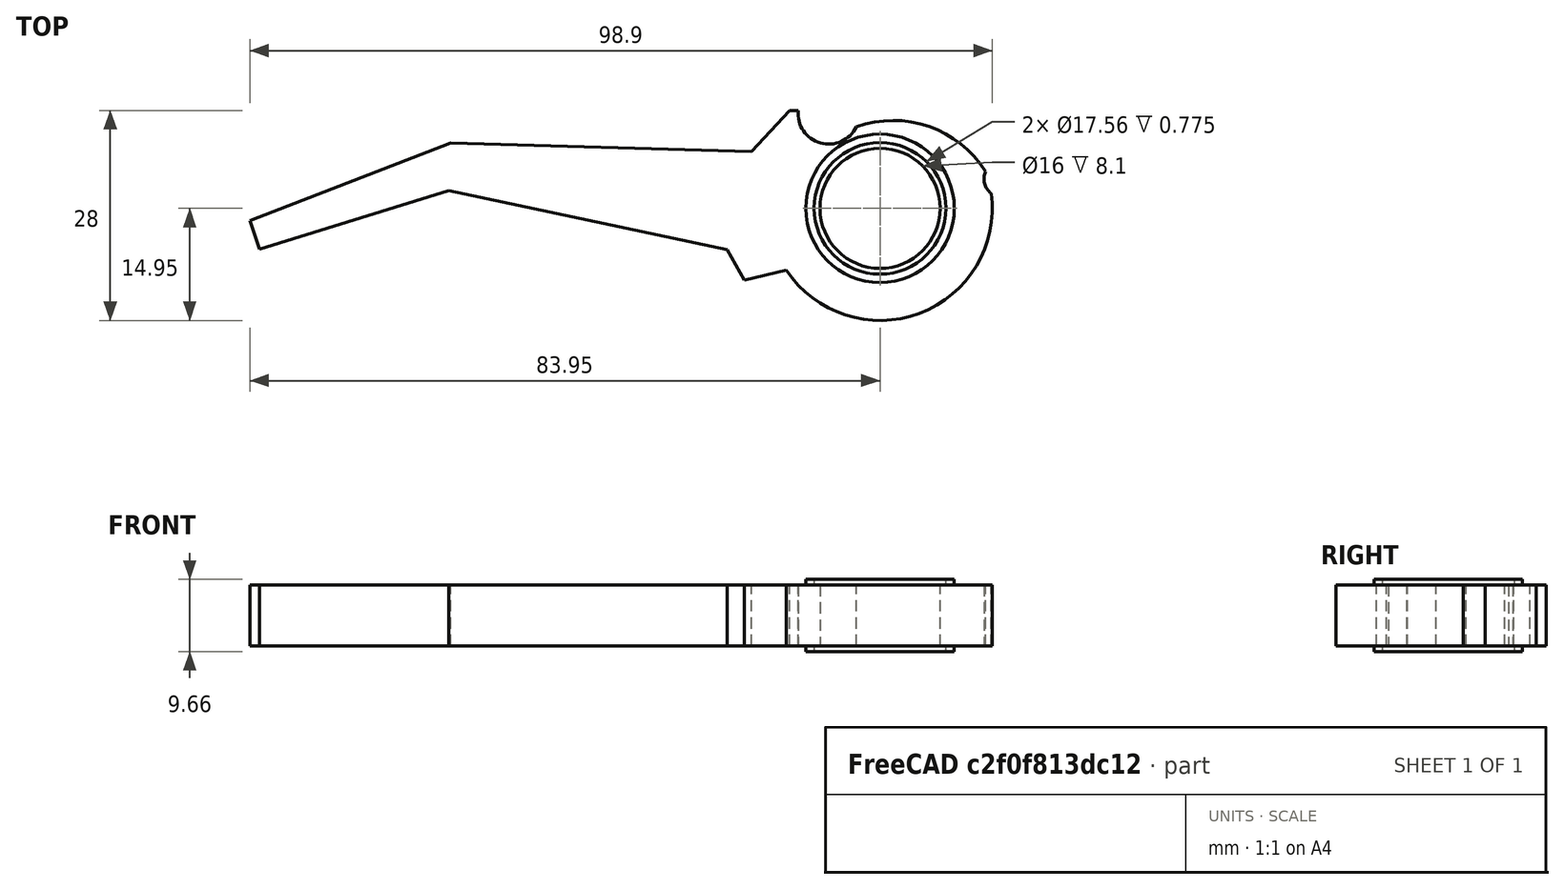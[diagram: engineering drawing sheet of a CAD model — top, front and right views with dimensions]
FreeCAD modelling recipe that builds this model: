
FCSTD DOCUMENT  (FreeCAD 0.20R)
Label: handle
License: All rights reserved
LicenseURL: http://en.wikipedia.org/wiki/All_rights_reserved
objects: Sketcher::SketchObject×3, PartDesign::Pad×2, Image::ImagePlane×1, PartDesign::Body×1
note: 8 computed .brp shape members not serialized (recipe doc carries the construction recipe); baked Part::Feature solids carry a one-line shape summary decoded from their .brp

FEATURE [Image::ImagePlane] ImagePlane
  Placement = pos=(-40.85,-1.3,0) rot=(0,0,1;6.02139rad)
  XSize = 214.62
  YSize = 161.597
FEATURE [Sketcher::SketchObject] Sketch
  FullyConstrained = false
  sketch-geometry (16):
    g0: Circle CenterX=0 CenterY=0 CenterZ=0 NormalX=0 NormalY=0 NormalZ=1 AngleXU=0 Radius=8
    g1: Circle CenterX=0 CenterY=0 CenterZ=0 NormalX=0 NormalY=0 NormalZ=1 AngleXU=0 Radius=9.89235
    g2: ArcOfCircle CenterX=0 CenterY=0 CenterZ=0 NormalX=0 NormalY=0 NormalZ=1 AngleXU=0 Radius=14.9473 StartAngle=3.7254 EndAngle=6.41772
    g3: ArcOfCircle CenterX=-6.8226 CenterY=12.6564 CenterZ=0 NormalX=0 NormalY=0 NormalZ=1 AngleXU=0 Radius=4.09132 StartAngle=3.04456 EndAngle=5.8257
    g4: ArcOfCircle CenterX=1.77311 CenterY=-2.74076 CenterZ=0 NormalX=0 NormalY=0 NormalZ=1 AngleXU=0 Radius=14.455 StartAngle=0.556159 EndAngle=1.91848
    g5: ArcOfCircle CenterX=16.2043 CenterY=3.91639 CenterZ=0 NormalX=0 NormalY=0 NormalZ=1 AngleXU=0 Radius=2.36466 StartAngle=2.71703 EndAngle=4.08292
    g6: LineSegment StartX=-10.8947 StartY=13.0528 StartZ=0 EndX=-12.022 EndY=13.0528 EndZ=0
    g7: LineSegment StartX=-12.022 StartY=13.0528 StartZ=0 EndX=-17.151 EndY=7.54055 EndZ=0
    g8: LineSegment StartX=-17.151 StartY=7.54055 StartZ=0 EndX=-57.1729 EndY=8.74142 EndZ=0
    g9: LineSegment StartX=-12.4716 StartY=-8.23901 StartZ=0 EndX=-18.0787 EndY=-9.56692 EndZ=0
    g10: LineSegment StartX=-18.0787 StartY=-9.56692 StartZ=0 EndX=-20.3779 EndY=-5.48142 EndZ=0
    g11: LineSegment StartX=-20.3779 StartY=-5.48142 StartZ=0 EndX=-57.4195 EndY=2.37023 EndZ=0
    g12: LineSegment StartX=-57.4195 StartY=2.37023 StartZ=0 EndX=-82.6501 EndY=-5.46265 EndZ=0
    g13: LineSegment StartX=-82.6501 StartY=-5.46265 StartZ=0 EndX=-83.949 EndY=-1.60525 EndZ=0
    g14: LineSegment StartX=-83.949 StartY=-1.60525 StartZ=0 EndX=-57.1729 EndY=8.74142 EndZ=0
    g15: Circle CenterX=0 CenterY=0 CenterZ=0 NormalX=0 NormalY=0 NormalZ=1 AngleXU=0 Radius=8.7784
  constraints (18):
    c: Coincident(g0,g-1)
    c: Diameter(g0) = 16
    c: Coincident(g1,g0)
    c: Coincident(g2,g0)
    c: Coincident(g4,g3)
    c: Coincident(g5,g4)
    c: Coincident(g5,g2)
    c: Coincident(g6,g3)
    c: Horizontal(g6)
    c: Coincident(g7,g6)
    c: Coincident(g8,g7)
    c: Coincident(g9,g2)
    c: Coincident(g10,g9)
    c: Coincident(g11,g10)
    c: Coincident(g13,g12)
    c: Coincident(g14,g13)
    c: Coincident(g14,g8)
    c: Coincident(g15,g0)
FEATURE [Sketcher::SketchObject] Sketch001
  FullyConstrained = false
  sketch-geometry (14):
    g0: Circle CenterX=0 CenterY=0 CenterZ=0 NormalX=0 NormalY=0 NormalZ=1 AngleXU=0 Radius=8
    g1: ArcOfCircle CenterX=0 CenterY=0 CenterZ=0 NormalX=0 NormalY=0 NormalZ=1 AngleXU=0 Radius=14.9473 StartAngle=3.7254 EndAngle=6.41772
    g2: ArcOfCircle CenterX=-6.8226 CenterY=12.6564 CenterZ=0 NormalX=0 NormalY=0 NormalZ=1 AngleXU=0 Radius=4.09132 StartAngle=3.04456 EndAngle=5.8257
    g3: ArcOfCircle CenterX=1.77311 CenterY=-2.74076 CenterZ=0 NormalX=0 NormalY=0 NormalZ=1 AngleXU=0 Radius=14.455 StartAngle=0.556159 EndAngle=1.91848
    g4: ArcOfCircle CenterX=16.2043 CenterY=3.91639 CenterZ=0 NormalX=0 NormalY=0 NormalZ=1 AngleXU=0 Radius=2.36466 StartAngle=2.71703 EndAngle=4.08292
    g5: LineSegment StartX=-10.8947 StartY=13.0528 StartZ=0 EndX=-12.022 EndY=13.0528 EndZ=0
    g6: LineSegment StartX=-12.022 StartY=13.0528 StartZ=0 EndX=-17.151 EndY=7.54055 EndZ=0
    g7: LineSegment StartX=-17.151 StartY=7.54055 StartZ=0 EndX=-57.1729 EndY=8.74142 EndZ=0
    g8: LineSegment StartX=-12.4716 StartY=-8.23901 StartZ=0 EndX=-18.0787 EndY=-9.56692 EndZ=0
    g9: LineSegment StartX=-18.0787 StartY=-9.56692 StartZ=0 EndX=-20.3779 EndY=-5.48142 EndZ=0
    g10: LineSegment StartX=-20.3779 StartY=-5.48142 StartZ=0 EndX=-57.4195 EndY=2.37023 EndZ=0
    g11: LineSegment StartX=-57.4195 StartY=2.37023 StartZ=0 EndX=-82.6501 EndY=-5.46265 EndZ=0
    g12: LineSegment StartX=-82.6501 StartY=-5.46265 StartZ=0 EndX=-83.949 EndY=-1.60525 EndZ=0
    g13: LineSegment StartX=-83.949 StartY=-1.60525 StartZ=0 EndX=-57.1729 EndY=8.74142 EndZ=0
  constraints (16):
    c: Coincident(g0,g-1)
    c: Diameter(g0) = 16
    c: Coincident(g1,g0)
    c: Coincident(g3,g2)
    c: Coincident(g4,g3)
    c: Coincident(g4,g1)
    c: Coincident(g5,g2)
    c: Horizontal(g5)
    c: Coincident(g6,g5)
    c: Coincident(g7,g6)
    c: Coincident(g8,g1)
    c: Coincident(g9,g8)
    c: Coincident(g10,g9)
    c: Coincident(g12,g11)
    c: Coincident(g13,g12)
    c: Coincident(g13,g7)
FEATURE [Sketcher::SketchObject] Sketch002
  FullyConstrained = false
  sketch-geometry (2):
    g0: Circle CenterX=0 CenterY=0 CenterZ=0 NormalX=0 NormalY=0 NormalZ=1 AngleXU=0 Radius=9.89235
    g1: Circle CenterX=0 CenterY=0 CenterZ=0 NormalX=0 NormalY=0 NormalZ=1 AngleXU=0 Radius=8.7784
FEATURE [PartDesign::Pad] Pad
  Direction = (0,0,1)
  Length = 8.1
  Length2 = 10
  Midplane = true
  Profile = -> Sketch001
  ReferenceAxis = -> Sketch001 [N_Axis]
  Type = 0
FEATURE [PartDesign::Pad] Pad001
  BaseFeature = -> Pad
  Direction = (0,0,1)
  Length = 9.65
  Length2 = 10
  Midplane = true
  Profile = -> Sketch002
  ReferenceAxis = -> Sketch002 [N_Axis]
  Type = 0
FEATURE [PartDesign::Body] Body
  Group = -> [Sketch,Sketch001,Sketch002,Pad,Pad001]
  Origin = -> Origin
  Tip = -> Pad001
